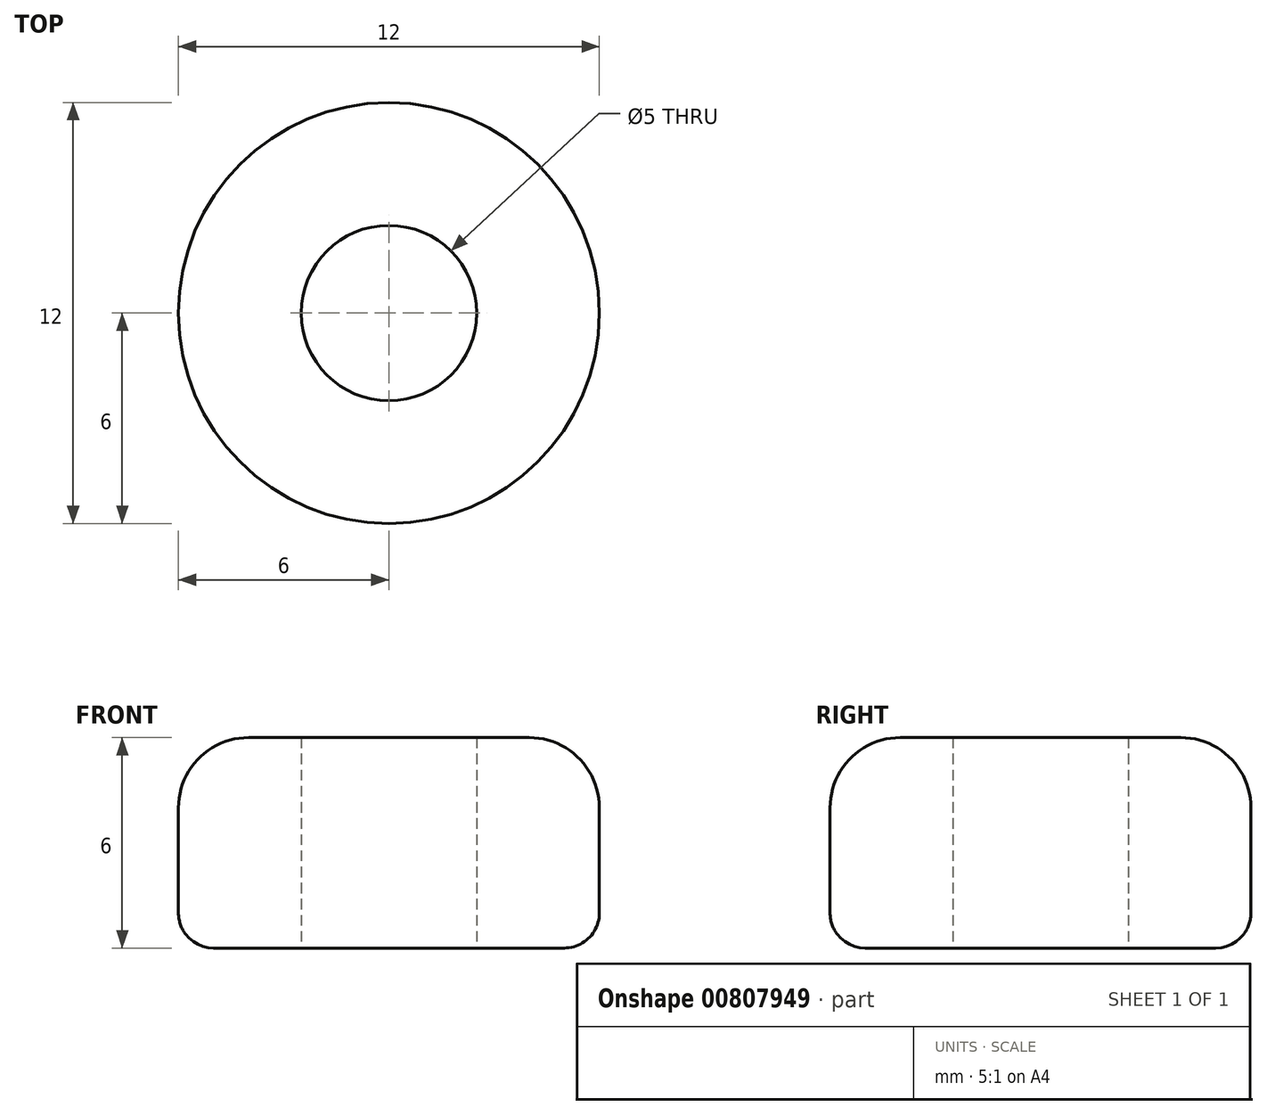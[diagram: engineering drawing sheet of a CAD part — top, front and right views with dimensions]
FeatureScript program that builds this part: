
annotation { "Feature Type Name" : "Feature", "Feature Type Description" : "" }
export const myFeature = defineFeature(function(context is Context, id is Id, definition is map)
    precondition{}
    {
        {
            var Q0;
            Q0=qCreatedBy(makeId("Top.planeOp"),FACE);
            var sketch = newSketch(context, id + "F0", { "sketchPlane" : qUnion([Q0])});
            skCircle(sketch, "E0", {"center": v(0, 0) * mm, "radius": 6 * mm});
            skSolve(sketch);
        }
        {
            var Q0;
            Q0 = qSketchRegion(id + "F0", true);
            var sketch = newSketch(context, id + "F1", { "sketchPlane" : qUnion([Q0])});
            skCircle(sketch, "E1", {"center": v(0, 0) * mm, "radius": 2.5 * mm});
            skSolve(sketch);
        }
        {
            var Q0;
            Q0=makeQuery(id+"F1.imprint","IMPRINT",FACE,{"disambiguationData":[TD([[makeQuery(id+"F1.imprint","IMPRINT",EDGE,{"derivedFrom":sQuery(id+"F1.wireOp",EDGE,"E1")}),-1.0]])]});
            extrude(context, id + "F2", {"entities" : qUnion([Q0]), "depth" : 6 * mm, "offsetDistance" : 25.4 * mm});
        }
        {
            var Q0;
            Q0=makeQuery(id+"F2.opExtrude","CAP_EDGE",EDGE,{"disambiguationData":[OSD([sQuery(id+"F0.wireOp",EDGE,"E0")])],"isStart":false});
            fillet(context, id + "F3", {"entities" : qUnion([Q0]), "radius" : 2 * mm, "tangentPropagation" : true, "allowEdgeOverflow" : false});
        }
        {
            var Q0;
            Q0=makeQuery(id+"F2.opExtrude","CAP_EDGE",EDGE,{"disambiguationData":[OSD([sQuery(id+"F0.wireOp",EDGE,"E0")])],"isStart":true});
            fillet(context, id + "F4", {"entities" : qUnion([Q0]), "radius" : 1 * mm, "tangentPropagation" : true, "allowEdgeOverflow" : false});
        }
    });
